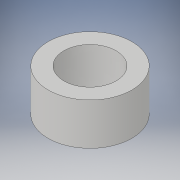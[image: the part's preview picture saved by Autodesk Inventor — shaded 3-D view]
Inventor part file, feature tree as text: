
AUTODESK INVENTOR PART (.ipt)
format: ipt  version: 2019 (Build 230136000, 136)  size: 94,720 bytes
history: native  units: in
note: dims shown in document units (in); Inventor stores cm internally (conversion verified against a paired STEP export)
features: extrude x1, sketch x1
ambient origin geometry x8: Origin, YZ Plane, XZ Plane, XY Plane, X Axis, Y Axis, Z Axis, Center Point
bodies: Solid1 (feature_tree)
feature tree (2):
  extrude  "Extrusion1"  Depth=0.5in
  sketch  "Sketch1"  dims[d0=0.625in d1=1.0in d2=0.5in d3=0.0in]
